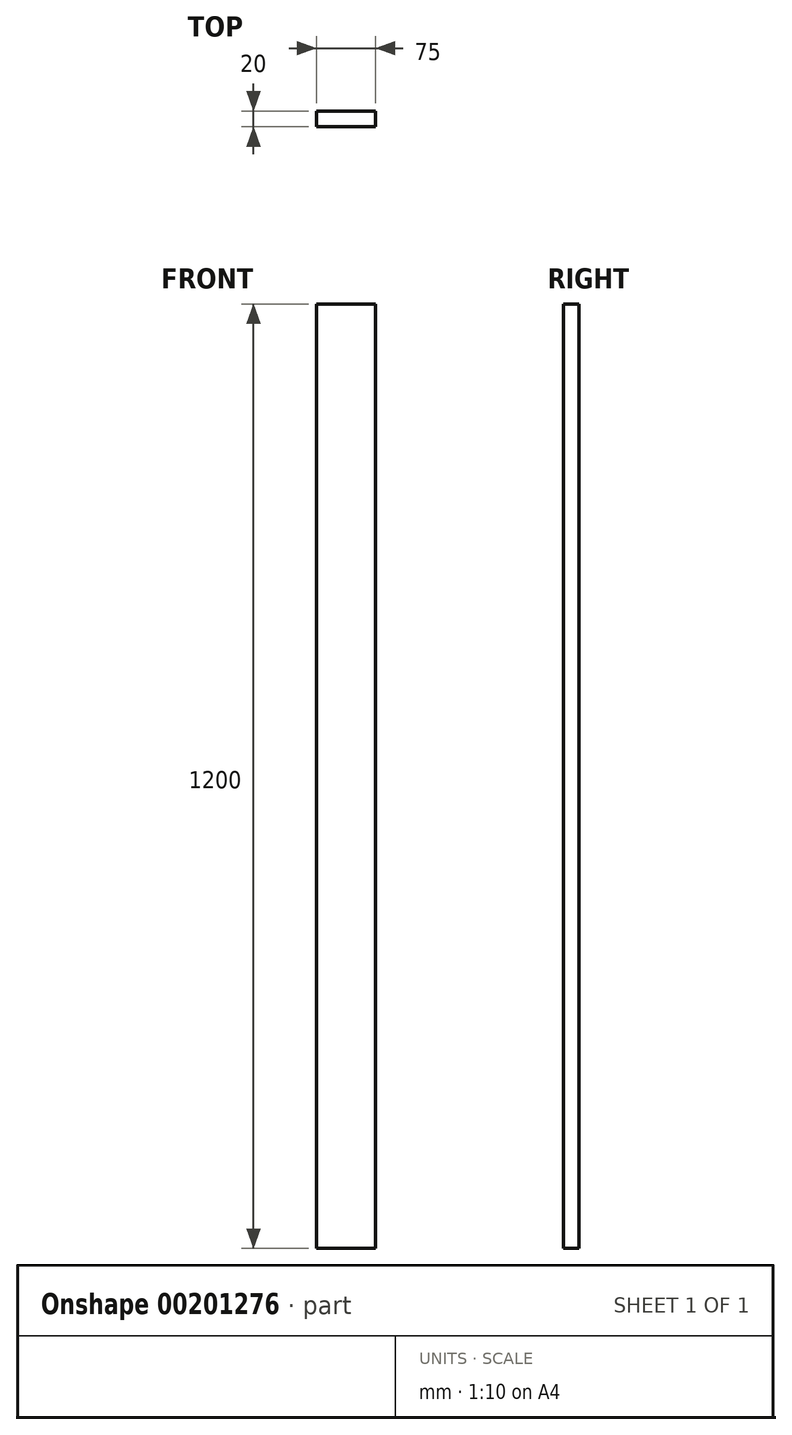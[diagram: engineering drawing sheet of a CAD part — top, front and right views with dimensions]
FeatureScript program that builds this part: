
annotation { "Feature Type Name" : "Feature", "Feature Type Description" : "" }
export const myFeature = defineFeature(function(context is Context, id is Id, definition is map)
    precondition{}
    {
        {
            var Q0;
            Q0=qCreatedBy(makeId("Top.planeOp"),FACE);
            var sketch = newSketch(context, id + "F0", { "sketchPlane" : qUnion([Q0])});
            skLineSegment(sketch, "E0.bottom", {"start": v(0, 0) * mm, "end": v(75, 0) * mm});
            skLineSegment(sketch, "E0.top", {"start": v(0, 20) * mm, "end": v(75, 20) * mm});
            skLineSegment(sketch, "E0.left", {"start": v(0, 0) * mm, "end": v(0, 20) * mm});
            skLineSegment(sketch, "E0.right", {"start": v(75, 0) * mm, "end": v(75, 20) * mm});
            skSolve(sketch);
        }
        {
            var Q0;
            Q0=qSketchRegion(id+"F0",true);
            extrude(context, id + "F1", {"entities" : qUnion([Q0]), "depth" : 1200 * mm});
        }
    });
